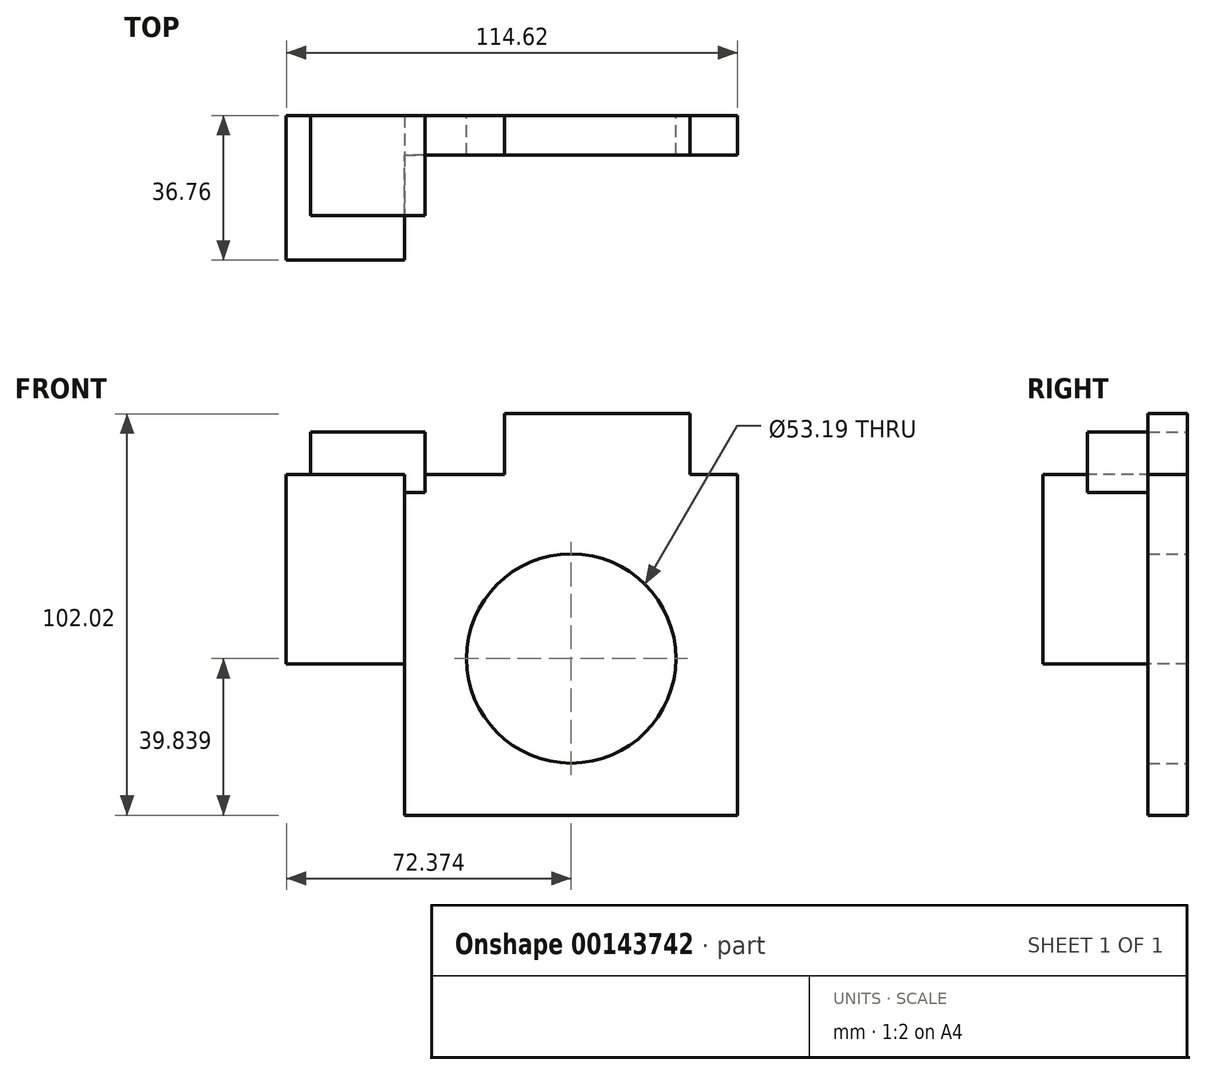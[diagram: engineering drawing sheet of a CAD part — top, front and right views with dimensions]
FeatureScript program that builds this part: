
annotation { "Feature Type Name" : "Feature", "Feature Type Description" : "" }
export const myFeature = defineFeature(function(context is Context, id is Id, definition is map)
    precondition{}
    {
        {
            var Q0;
            Q0=qCreatedBy(makeId("Front.planeOp"),FACE);
            var sketch = newSketch(context, id + "F0", { "sketchPlane" : qUnion([Q0])});
            skLineSegment(sketch, "E0.bottom", {"start": v(-37.16, 38.97) * mm, "end": v(47.46, 38.97) * mm});
            skLineSegment(sketch, "E0.top", {"start": v(-37.16, -47.66) * mm, "end": v(47.46, -47.66) * mm});
            skLineSegment(sketch, "E0.left", {"start": v(-37.16, 38.97) * mm, "end": v(-37.16, -47.66) * mm});
            skLineSegment(sketch, "E0.right", {"start": v(47.46, 38.97) * mm, "end": v(47.46, -47.66) * mm});
            skCircle(sketch, "E1", {"center": v(5.21, -7.82) * mm, "radius": 26.6 * mm});
            skSolve(sketch);
        }
        {
            var Q0;
            Q0 = qSketchRegion(id + "F0", true);
            var Q1;
            Q1=makeQuery(id+"F0.imprint","IMPRINT",FACE,{"disambiguationData":[TD([[makeQuery(id+"F0.imprint","IMPRINT",EDGE,{"derivedFrom":sQuery(id+"F0.wireOp",EDGE,"E0.bottom")}),-1.0]])]});
            extrude(context, id + "F1", {"entities" : qUnion([Q0, Q1]), "depth" : 10 * mm});
        }
        {
            var Q0;
            Q0=makeQuery(id+"F1.opExtrude","SWEPT_FACE",FACE,{"disambiguationData":[OSD([sQuery(id+"F0.wireOp",EDGE,"E0.left")])]});
            var sketch = newSketch(context, id + "F2", { "sketchPlane" : qUnion([Q0])});
            skLineSegment(sketch, "E2.bottom", {"start": v(-28.28, 38.97) * mm, "end": v(36.76, 38.97) * mm});
            skLineSegment(sketch, "E2.top", {"start": v(-28.28, -9.22) * mm, "end": v(36.76, -9.22) * mm});
            skLineSegment(sketch, "E2.left", {"start": v(-28.28, 38.97) * mm, "end": v(-28.28, -9.22) * mm});
            skLineSegment(sketch, "E2.right", {"start": v(36.76, 38.97) * mm, "end": v(36.76, -9.22) * mm});
            skSolve(sketch);
        }
        {
            var Q0;
            {var subQ3=sQuery(id+"F2.wireOp",EDGE,"E2.right");Q0=makeQuery(id+"F2.imprint","IMPRINT",FACE,{"disambiguationData":[TD([[makeQuery(id+"F2.imprint","IMPRINT",EDGE,{"derivedFrom":subQ3}),-1.0]])]});}
            var Q1;
            {var subQ0=sQuery(id+"F2.wireOp",EDGE,"E2.bottom");var subQ1=sQuery(id+"F0.wireOp",EDGE,"E0.left");var subQ2=makeQuery(id+"F1.opExtrude","CAP_EDGE",EDGE,{"disambiguationData":[OSD([subQ1])],"isStart":true});var subQ3=makeQuery(id+"F2.imprint","INTERSECT",VERTEX,{"derivedFrom":[subQ2,subQ0]});var subQ4=makeQuery(id+"F1.opExtrude","CAP_EDGE",EDGE,{"disambiguationData":[OSD([subQ1])],"isStart":false});var subQ5=makeQuery(id+"F2.imprint","INTERSECT",VERTEX,{"derivedFrom":[subQ4,subQ0]});Q1=makeQuery(id+"F2.imprint","IMPRINT",FACE,{"disambiguationData":[TD([[makeQuery(id+"F2.imprint","IMPRINT",EDGE,{"disambiguationData":[TD([[subQ3,1.0],[subQ5,-1.0]])],"derivedFrom":subQ0}),1.0]])]});}
            extrude(context, id + "F3", {"entities" : qUnion([Q0, Q1]), "operationType" : NewBodyOperationType.ADD, "depth" : 30 * mm});
        }
        {
            var Q0;
            Q0=qCreatedBy(makeId("Front.planeOp"),FACE);
            var sketch = newSketch(context, id + "F4", { "sketchPlane" : qUnion([Q0])});
            skLineSegment(sketch, "E3.bottom", {"start": v(-61, 34.3) * mm, "end": v(-31.97, 34.3) * mm});
            skLineSegment(sketch, "E3.top", {"start": v(-61, 49.68) * mm, "end": v(-31.97, 49.68) * mm});
            skLineSegment(sketch, "E3.left", {"start": v(-61, 34.3) * mm, "end": v(-61, 49.68) * mm});
            skLineSegment(sketch, "E3.right", {"start": v(-31.97, 34.3) * mm, "end": v(-31.97, 49.68) * mm});
            skSolve(sketch);
        }
        {
            var Q0;
            Q0 = qSketchRegion(id + "F4", true);
            var Q1;
            Q1=makeQuery(id+"F4.imprint","IMPRINT",FACE,{"disambiguationData":[TD([[makeQuery(id+"F4.imprint","IMPRINT",EDGE,{"derivedFrom":sQuery(id+"F4.wireOp",EDGE,"E3.bottom")}),1.0]])]});
            extrude(context, id + "F5", {"entities" : qUnion([Q0, Q1]), "operationType" : NewBodyOperationType.ADD, "depth" : 25.4 * mm});
        }
        {
            var Q0;
            Q0=qCreatedBy(makeId("Front.planeOp"),FACE);
            var sketch = newSketch(context, id + "F6", { "sketchPlane" : qUnion([Q0])});
            skLineSegment(sketch, "E4.bottom", {"start": v(-11.72, 54.36) * mm, "end": v(35.39, 54.36) * mm});
            skLineSegment(sketch, "E4.top", {"start": v(-11.72, 35.68) * mm, "end": v(35.39, 35.68) * mm});
            skLineSegment(sketch, "E4.left", {"start": v(-11.72, 54.36) * mm, "end": v(-11.72, 35.68) * mm});
            skLineSegment(sketch, "E4.right", {"start": v(35.39, 54.36) * mm, "end": v(35.39, 35.68) * mm});
            skSolve(sketch);
        }
        {
            var Q0;
            Q0 = qSketchRegion(id + "F6", true);
            extrude(context, id + "F7", {"entities" : qUnion([Q0]), "operationType" : NewBodyOperationType.ADD, "depth" : 10 * mm});
        }
    });
